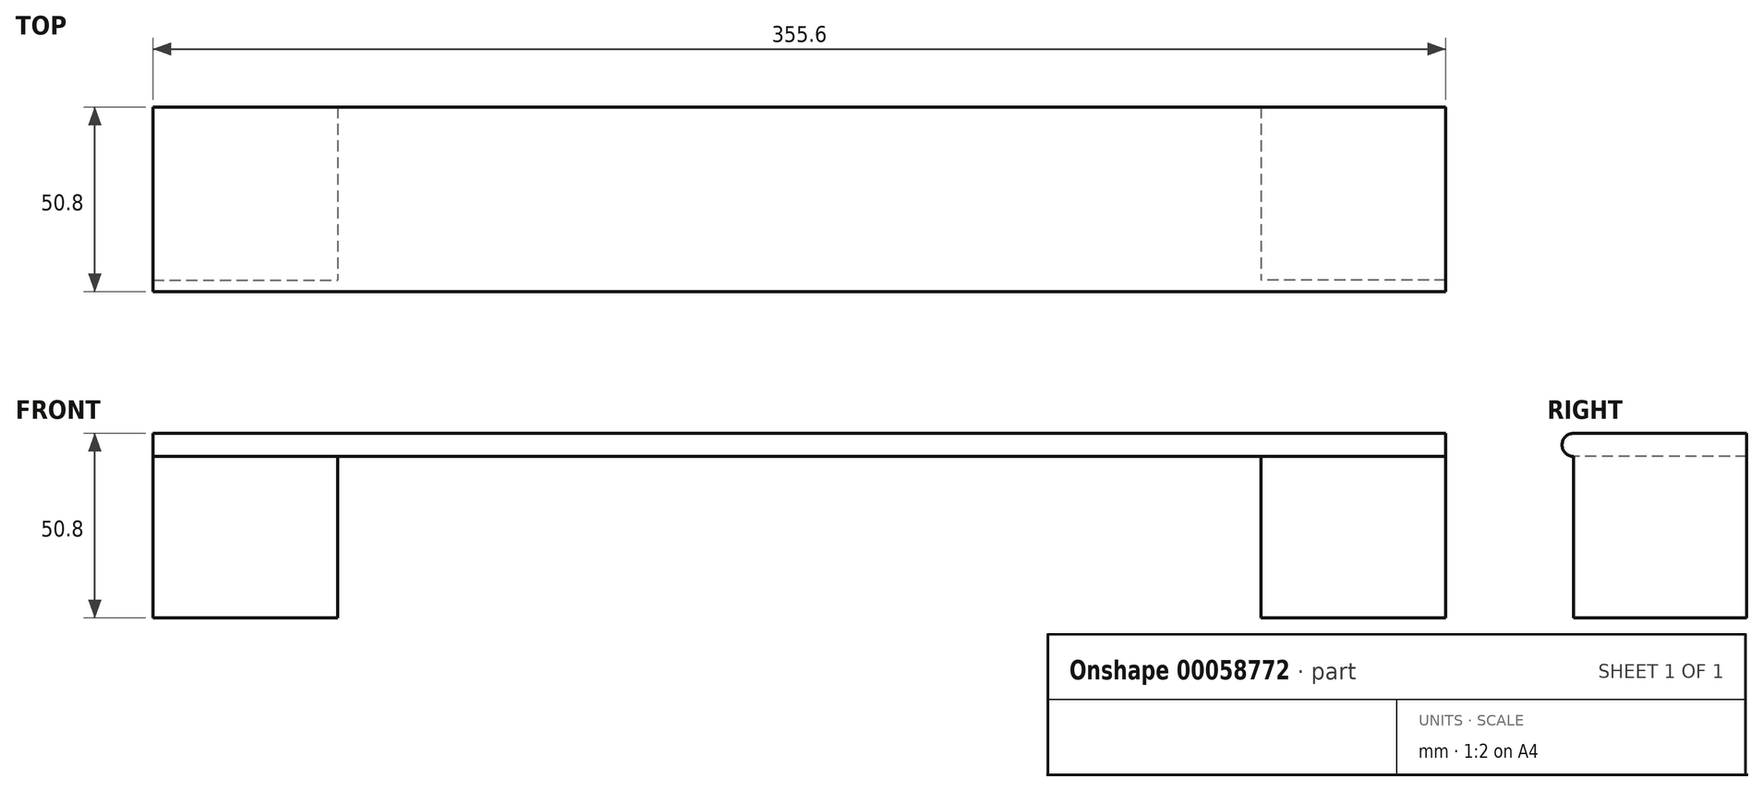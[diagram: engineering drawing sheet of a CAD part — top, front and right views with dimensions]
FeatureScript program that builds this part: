
annotation { "Feature Type Name" : "Feature", "Feature Type Description" : "" }
export const myFeature = defineFeature(function(context is Context, id is Id, definition is map)
    precondition{}
    {
        {
            var Q0;
            Q0=qCreatedBy(makeId("Right.planeOp"),FACE);
            var sketch = newSketch(context, id + "F0", { "sketchPlane" : qUnion([Q0])});
            skLineSegment(sketch, "E0.rect.bottom", {"start": v(25.4, 3.18) * mm, "end": v(-25.4, 3.18) * mm});
            skLineSegment(sketch, "E0.rect.top", {"start": v(25.4, -3.18) * mm, "end": v(-25.4, -3.18) * mm});
            skLineSegment(sketch, "E0.rect.left", {"start": v(25.4, 3.18) * mm, "end": v(25.4, -3.18) * mm});
            skLineSegment(sketch, "E0.rect.right", {"start": v(-25.4, 3.18) * mm, "end": v(-25.4, -3.18) * mm});
            skPoint(sketch, "E0.rect.middle", {"position": v(0, 0) * mm});
            skSolve(sketch);
        }
        {
            var Q0;
            Q0 = qSketchRegion(id + "F0", true);
            extrude(context, id + "F1", {"entities" : qUnion([Q0]), "depth" : 254 * mm});
        }
        {
            var Q0;
            Q0=makeQuery(id+"F1.opExtrude","SWEPT_EDGE",EDGE,{"disambiguationData":[OSD([sQuery(id+"F0.wireOp",EDGE,"E0.rect.bottom"),sQuery(id+"F0.wireOp",EDGE,"E0.rect.right")])]});
            var Q1;
            Q1=makeQuery(id+"F1.opExtrude","SWEPT_EDGE",EDGE,{"disambiguationData":[OSD([sQuery(id+"F0.wireOp",EDGE,"E0.rect.top"),sQuery(id+"F0.wireOp",EDGE,"E0.rect.right")])]});
            fillet(context, id + "F2", {"entities" : qUnion([Q0, Q1]), "radius" : 3.17 * mm, "tangentPropagation" : true, "allowEdgeOverflow" : false});
        }
        {
            var Q0;
            Q0=makeQuery(id+"F1.opExtrude","CAP_FACE",FACE,{"disambiguationData":[OSD([sQuery(id+"F0.wireOp",EDGE,"E0.rect.bottom"),sQuery(id+"F0.wireOp",EDGE,"E0.rect.top"),sQuery(id+"F0.wireOp",EDGE,"E0.rect.left"),sQuery(id+"F0.wireOp",EDGE,"E0.rect.right")])],"isStart":true});
            var sketch = newSketch(context, id + "F3", { "sketchPlane" : qUnion([Q0])});
            skLineSegment(sketch, "E1.bottom", {"start": v(22.23, 3.18) * mm, "end": v(-25.4, 3.18) * mm});
            skLineSegment(sketch, "E1.top", {"start": v(22.23, -47.62) * mm, "end": v(-25.4, -47.62) * mm});
            skLineSegment(sketch, "E1.left", {"start": v(22.23, 3.17) * mm, "end": v(22.23, -47.62) * mm});
            skLineSegment(sketch, "E1.right", {"start": v(-25.4, 3.17) * mm, "end": v(-25.4, -47.62) * mm});
            skSolve(sketch);
        }
        {
            var Q0;
            Q0 = qSketchRegion(id + "F3", true);
            extrude(context, id + "F4", {"entities" : qUnion([Q0]), "operationType" : NewBodyOperationType.ADD, "depth" : 50.8 * mm, "offsetDistance" : 25.4 * mm});
        }
        {
            var Q0;
            Q0=makeQuery(id+"F1.opExtrude","CAP_FACE",FACE,{"disambiguationData":[OSD([sQuery(id+"F0.wireOp",EDGE,"E0.rect.bottom"),sQuery(id+"F0.wireOp",EDGE,"E0.rect.top"),sQuery(id+"F0.wireOp",EDGE,"E0.rect.left"),sQuery(id+"F0.wireOp",EDGE,"E0.rect.right")])],"isStart":true});
            var sketch = newSketch(context, id + "F5", { "sketchPlane" : qUnion([Q0])});
            skArc(sketch, "E2.0.0", {"start": v(22.23, -3.18) * mm, "mid": v(25.4, 0) * mm, "end": v(22.23, 3.17) * mm});
            skLineSegment(sketch, "E2.0.1", {"start": v(22.23, 3.17) * mm, "end": v(22.23, -3.18) * mm});
            skSolve(sketch);
        }
        {
            var Q0;
            Q0 = qSketchRegion(id + "F5", true);
            var Q1;
            Q1=makeQuery(id+"F4.opExtrude","CAP_FACE",FACE,{"disambiguationData":[OSD([sQuery(id+"F3.wireOp",EDGE,"E1.bottom"),sQuery(id+"F3.wireOp",EDGE,"E1.top"),sQuery(id+"F3.wireOp",EDGE,"E1.left"),sQuery(id+"F3.wireOp",EDGE,"E1.right")])],"isStart":false});
            extrude(context, id + "F6", {"entities" : qUnion([Q0]), "operationType" : NewBodyOperationType.ADD, "endBound" : BoundingType.UP_TO_SURFACE, "depth" : 25.4 * mm, "endBoundEntityFace" : qUnion([Q1]), "offsetDistance" : 25.4 * mm});
        }
        {
            var Q0;
            Q0=makeQuery(id+"F1.opExtrude","CAP_FACE",FACE,{"disambiguationData":[OSD([sQuery(id+"F0.wireOp",EDGE,"E0.rect.bottom"),sQuery(id+"F0.wireOp",EDGE,"E0.rect.top"),sQuery(id+"F0.wireOp",EDGE,"E0.rect.left"),sQuery(id+"F0.wireOp",EDGE,"E0.rect.right")])],"isStart":false});
            var sketch = newSketch(context, id + "F7", { "sketchPlane" : qUnion([Q0])});
            skLineSegment(sketch, "E3.0.0", {"start": v(-22.23, -47.62) * mm, "end": v(-22.23, -3.18) * mm});
            skArc(sketch, "E3.0.1", {"start": v(-22.23, -3.18) * mm, "mid": v(-25.4, 0) * mm, "end": v(-22.23, 3.17) * mm});
            skLineSegment(sketch, "E3.0.2", {"start": v(-22.23, 3.18) * mm, "end": v(25.4, 3.18) * mm});
            skLineSegment(sketch, "E3.0.3", {"start": v(25.4, 3.17) * mm, "end": v(25.4, -47.62) * mm});
            skLineSegment(sketch, "E3.0.4", {"start": v(25.4, -47.62) * mm, "end": v(-22.23, -47.62) * mm});
            skSolve(sketch);
        }
        {
            var Q0;
            Q0 = qSketchRegion(id + "F7", true);
            extrude(context, id + "F8", {"entities" : qUnion([Q0]), "operationType" : NewBodyOperationType.ADD, "depth" : 50.8 * mm, "offsetDistance" : 25.4 * mm});
        }
    });
